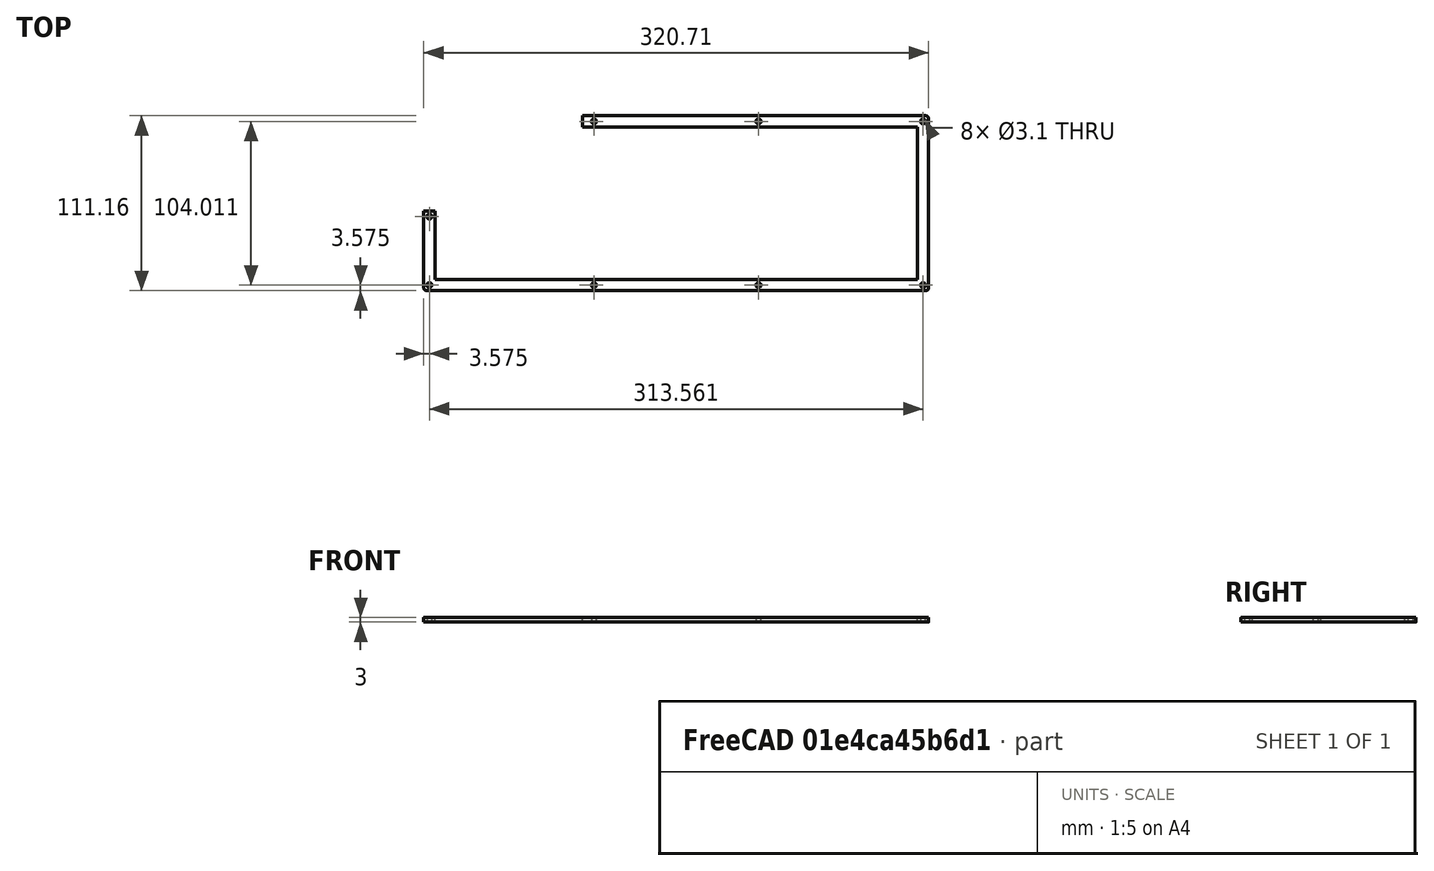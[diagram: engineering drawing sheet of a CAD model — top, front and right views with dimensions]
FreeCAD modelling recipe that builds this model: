
FCSTD DOCUMENT  (FreeCAD 0.19R24366 (Git))
Label: top_layer
License: All rights reserved
LicenseURL: http://en.wikipedia.org/wiki/All_rights_reserved
objects: Sketcher::SketchObject×1, PartDesign::Pad×1, PartDesign::Body×1, PartDesign::CoordinateSystem×1, App::Part×1
note: 5 computed .brp shape members not serialized (recipe doc carries the construction recipe); baked Part::Feature solids carry a one-line shape summary decoded from their .brp
EXTERNAL_REF file=../master.FCStd obj=Spreadsheet

FEATURE [Sketcher::SketchObject] Sketch  label="top_layer_sketch"
  FullyConstrained = true
  MapMode = 5
  Support = -> [XY_Plane001]
  expr: Constraints[80] = <<master>>#<<inputs>>.wall_thickness
  expr: Constraints[61] = 0
  expr: Constraints[81] = <<master>>#<<inputs>>.wall_thickness
  expr: Constraints[66] = <<master>>#<<inputs>>.top_edge_padding - <<master>>#<<inputs>>.wall_thickness / 2
  expr: Constraints[8] = <<master>>#<<inputs>>.key_width
  expr: Constraints[56] = <<master>>#<<inputs>>.right_edge_padding
  expr: Constraints[82] = <<master>>#<<inputs>>.wall_thickness
  expr: Constraints[94] = <<master>>#<<inputs>>.wall_thickness
  expr: Constraints[53] = (<<master>>#<<inputs>>.key_height + <<master>>#<<inputs>>.vertical_key_spacing) * 4 + <<master>>#<<inputs>>.bottom_edge_padding - <<master>>#<<inputs>>.wall_thickness / 2 + <<master>>#<<inputs>>.key_height
  expr: Constraints[78] = <<master>>#<<inputs>>.wall_thickness / 2
  expr: Constraints[91] = <<master>>#<<inputs>>.wall_thickness / 2
  expr: Constraints[98] = <<master>>#<<inputs>>.hyperpixel_width
  expr: Constraints[77] = <<master>>#<<inputs>>.wall_thickness / 2
  expr: Constraints[22] = (<<master>>#<<inputs>>.key_width + <<master>>#<<inputs>>.horizontal_key_spacing) * 15
  expr: Constraints[55] = <<master>>#<<inputs>>.left_edge_padding - <<master>>#<<inputs>>.wall_thickness / 2
  expr: Constraints[9] = <<master>>#<<inputs>>.key_height
  expr: Constraints[46] = <<master>>#<<inputs>>.edge_fillet_radius
  expr: Constraints[49] = <<master>>#<<inputs>>.mounting_hole_diameter / 2
  expr: Constraints[58] = <<master>>#<<inputs>>.wall_thickness / 2
  expr: Constraints[71] = 0
  expr: Constraints[35] = (<<master>>#<<inputs>>.key_height + <<master>>#<<inputs>>.vertical_key_spacing) * 4
  expr: Constraints[60] = 0
  expr: Constraints[62] = ((<<master>>#<<inputs>>.key_width + <<master>>#<<inputs>>.horizontal_key_spacing) * 15 + <<master>>#<<inputs>>.key_width + <<master>>#<<inputs>>.right_edge_padding - <<master>>#<<inputs>>.wall_thickness / 2 + <<master>>#<<inputs>>.left_edge_padding - <<master>>#<<inputs>>.wall_thickness / 2) / 3
  expr: Constraints[85] = <<master>>#<<inputs>>.wall_thickness
  expr: Constraints[54] = <<master>>#<<inputs>>.bottom_edge_padding
  expr: Constraints[59] = ((<<master>>#<<inputs>>.key_width + <<master>>#<<inputs>>.horizontal_key_spacing) * 15 + <<master>>#<<inputs>>.key_width + <<master>>#<<inputs>>.right_edge_padding - <<master>>#<<inputs>>.wall_thickness / 2 + <<master>>#<<inputs>>.left_edge_padding - <<master>>#<<inputs>>.wall_thickness / 2) / 3
  expr: Constraints[73] = 0
  expr: Constraints[74] = (<<master>>#<<inputs>>.key_height + <<master>>#<<inputs>>.vertical_key_spacing) * 3 - <<master>>#<<inputs>>.wall_thickness / 2
  sketch-geometry (35):
    g0: LineSegment StartX=-7 StartY=7 StartZ=0 EndX=7 EndY=7 EndZ=0
    g1: LineSegment StartX=7 StartY=7 StartZ=0 EndX=7 EndY=-7 EndZ=0
    g2: LineSegment StartX=7 StartY=-7 StartZ=0 EndX=-7 EndY=-7 EndZ=0
    g3: LineSegment StartX=-7 StartY=-7 StartZ=0 EndX=-7 EndY=7 EndZ=0
    g4: LineSegment StartX=278.75 StartY=7 StartZ=0 EndX=292.75 EndY=7 EndZ=0
    g5: LineSegment StartX=292.75 StartY=7 StartZ=0 EndX=292.75 EndY=-7 EndZ=0
    g6: LineSegment StartX=292.75 StartY=-7 StartZ=0 EndX=278.75 EndY=-7 EndZ=0
    g7: LineSegment StartX=278.75 StartY=-7 StartZ=0 EndX=278.75 EndY=7 EndZ=0
    g8: GeomPoint X=278.75 Y=7 Z=0
    g9: LineSegment StartX=-7 StartY=-69.2 StartZ=0 EndX=7 EndY=-69.2 EndZ=0
    g10: LineSegment StartX=7 StartY=-69.2 StartZ=0 EndX=7 EndY=-83.2 EndZ=0
    g11: LineSegment StartX=7 StartY=-83.2 StartZ=0 EndX=-7 EndY=-83.2 EndZ=0
    g12: LineSegment StartX=-7 StartY=-83.2 StartZ=0 EndX=-7 EndY=-69.2 EndZ=0
    g13: LineSegment StartX=83.5225 StartY=17.4775 StartZ=0 EndX=301.228 EndY=17.4775 EndZ=0
    g14: LineSegment StartX=303.228 StartY=15.4775 StartZ=0 EndX=303.228 EndY=-91.6775 EndZ=0
    g15: LineSegment StartX=301.228 StartY=-93.6775 StartZ=0 EndX=-15.4775 EndY=-93.6775 EndZ=0
    g16: LineSegment StartX=-17.4775 StartY=-91.6775 StartZ=0 EndX=-17.4775 EndY=-43.006 EndZ=0
    g17: ArcOfCircle CenterX=301.228 CenterY=15.4775 CenterZ=0 NormalX=0 NormalY=0 NormalZ=1 AngleXU=0 Radius=2 StartAngle=0 EndAngle=1.5708
    g18: ArcOfCircle CenterX=301.228 CenterY=-91.6775 CenterZ=0 NormalX=0 NormalY=0 NormalZ=1 AngleXU=0 Radius=2 StartAngle=4.71239 EndAngle=6.28319
    g19: ArcOfCircle CenterX=-15.4775 CenterY=-91.6775 CenterZ=0 NormalX=0 NormalY=0 NormalZ=1 AngleXU=0 Radius=2 StartAngle=3.14159 EndAngle=4.71239
    g20: Circle CenterX=-13.9055 CenterY=-90.1055 CenterZ=0 NormalX=0 NormalY=0 NormalZ=1 AngleXU=0 Radius=1.55
    g21: Circle CenterX=195.135 CenterY=-90.1055 CenterZ=0 NormalX=0 NormalY=0 NormalZ=1 AngleXU=0 Radius=1.55
    g22: Circle CenterX=299.656 CenterY=-90.1055 CenterZ=0 NormalX=0 NormalY=0 NormalZ=1 AngleXU=0 Radius=1.55
    g23: Circle CenterX=90.6148 CenterY=-90.1055 CenterZ=0 NormalX=0 NormalY=0 NormalZ=1 AngleXU=0 Radius=1.55
    g24: Circle CenterX=90.6148 CenterY=13.9055 CenterZ=0 NormalX=0 NormalY=0 NormalZ=1 AngleXU=0 Radius=1.55
    g25: Circle CenterX=195.135 CenterY=13.9055 CenterZ=0 NormalX=0 NormalY=0 NormalZ=1 AngleXU=0 Radius=1.55
    g26: Circle CenterX=299.656 CenterY=13.9055 CenterZ=0 NormalX=0 NormalY=0 NormalZ=1 AngleXU=0 Radius=1.55
    g27: Circle CenterX=-13.9055 CenterY=-46.578 CenterZ=0 NormalX=0 NormalY=0 NormalZ=1 AngleXU=0 Radius=1.55
    g28: LineSegment StartX=-17.4775 StartY=-43.006 StartZ=0 EndX=-10.3335 EndY=-43.006 EndZ=0
    g29: LineSegment StartX=-10.3335 StartY=-86.5335 StartZ=0 EndX=296.084 EndY=-86.5335 EndZ=0
    g30: LineSegment StartX=296.084 StartY=10.3335 StartZ=0 EndX=296.084 EndY=-86.5335 EndZ=0
    g31: LineSegment StartX=83.5225 StartY=10.3335 StartZ=0 EndX=296.084 EndY=10.3335 EndZ=0
    g32: LineSegment StartX=-10.3335 StartY=-43.006 StartZ=0 EndX=-10.3335 EndY=-86.5335 EndZ=0
    g33: LineSegment StartX=83.5225 StartY=17.4775 StartZ=0 EndX=83.5225 EndY=10.3335 EndZ=0
    g34: LineSegment StartX=-17.4775 StartY=-43.006 StartZ=0 EndX=80.5225 EndY=-43.006 EndZ=0
  constraints (100):
    c: Coincident(g0,g1)
    c: Coincident(g1,g2)
    c: Coincident(g2,g3)
    c: Coincident(g3,g0)
    c: Horizontal(g0)
    c: Horizontal(g2)
    c: Vertical(g1)
    c: Vertical(g3)
    c: Distance(g0) = 14
    c: Distance(g3) = 14
    c: Symmetric(g0,g1,g-1)
    c: Coincident(g4,g5)
    c: Coincident(g5,g6)
    c: Coincident(g6,g7)
    c: Coincident(g7,g4)
    c: Horizontal(g4)
    c: Horizontal(g6)
    c: Vertical(g5)
    c: Vertical(g7)
    c: Equal(g3,g7)
    c: Equal(g0,g4)
    c: DistanceY(g0,g8) = 0
    c: DistanceX(g0,g8) = 285.75
    c: Coincident(g4,g8)
    c: Coincident(g9,g10)
    c: Coincident(g10,g11)
    c: Coincident(g11,g12)
    c: Coincident(g12,g9)
    c: Horizontal(g9)
    c: Horizontal(g11)
    c: Vertical(g10)
    c: Vertical(g12)
    c: Equal(g0,g9)
    c: Equal(g3,g12)
    c: DistanceX(g0,g9) = 0
    c: DistanceY(g9,g0) = 76.2
    c: Horizontal(g13)
    c: Horizontal(g15)
    c: Vertical(g14)
    c: Vertical(g16)
    c: Tangent(g13,g17) = 1.5708
    c: Tangent(g14,g17) = 1.5708
    c: Tangent(g14,g18) = 1.5708
    c: Tangent(g15,g18) = 1.5708
    c: Tangent(g15,g19) = 1.5708
    c: Tangent(g16,g19) = 1.5708
    c: Radius(g19) = 2
    c: Equal(g19,g18)
    c: Equal(g17,g18)
    c: Radius(g20) = 1.55
    c: Equal(g20,g21)
    c: Equal(g21,g22)
    c: Equal(g21,g23)
    c: DistanceY(g20,g0) = 97.1055
    c: DistanceY(g15,g11) = 10.4775
    c: DistanceX(g20,g0) = 6.9055
    c: DistanceX(g4,g14) = 10.4775
    c: DistanceY(g20,g22) = 0
    c: DistanceX(g22,g14) = 3.572
    c: DistanceX(g20,g23) = 104.52
    c: DistanceY(g23,g20) = 0
    c: DistanceY(g23,g21) = 0
    c: DistanceX(g21,g22) = 104.52
    c: Equal(g21,g26)
    c: Equal(g26,g25)
    c: Equal(g26,g24)
    c: DistanceY(g8,g26) = 6.9055
    c: DistanceX(g26,g22) = 0
    c: DistanceX(g25,g21) = 0
    c: DistanceY(g25,g26) = 0
    c: DistanceX(g23,g24) = 0
    c: DistanceY(g24,g25) = 0
    c: Equal(g20,g27)
    c: DistanceX(g20,g27) = 0
    c: DistanceY(g27,g0) = 53.578
    c: Horizontal(g28)
    c: Coincident(g16,g28)
    c: DistanceX(g16,g27) = 3.572
    c: DistanceY(g26,g13) = 3.572
    c: Horizontal(g29)
    c: DistanceY(g15,g29) = 7.144
    c: DistanceX(g16,g29) = 7.144
    c: DistanceX(g29,g14) = 7.144
    c: Vertical(g30)
    c: Coincident(g30,g29)
    c: DistanceY(g30,g13) = 7.144
    c: Horizontal(g31)
    c: Coincident(g31,g30)
    c: Vertical(g32)
    c: Coincident(g32,g29)
    c: Coincident(g28,g32)
    c: DistanceY(g27,g28) = 3.572
    c: DistanceX(g13,g31) = 0
    c: Coincident(g33,g13)
    c: Distance(g33) = 7.144
    c: Perpendicular(g13,g33)
    c: Horizontal(g34)
    c: Coincident(g34,g16)
    c: Distance(g34) = 98
    c: DistanceX(g34,g31) = 3
FEATURE [PartDesign::Pad] Pad  label="top_layer_pad"
  Direction = (1,1,1)
  Length = 3
  Length2 = 100
  Profile = -> Sketch
  Type = 0
  expr: Length = <<master>>#<<inputs>>.top_layer_thickness
FEATURE [PartDesign::Body] Body  label="top_layer_body"
  Group = -> [Sketch,Pad]
  Origin = -> Origin001
  Tip = -> Pad
FEATURE [PartDesign::CoordinateSystem] top_left_lcs_closed_layer  label="top_layer_lcs"
  AttacherType = Attacher::AttachEngine3D
  MapMode = 5
  Placement = pos=(0,0,3) rot=(0,0,1;0rad)
  Support = -> [Pad]
FEATURE [App::Part] Part  label="top_layer_part"
  Group = -> [Body,top_left_lcs_closed_layer]
  Origin = -> Origin
